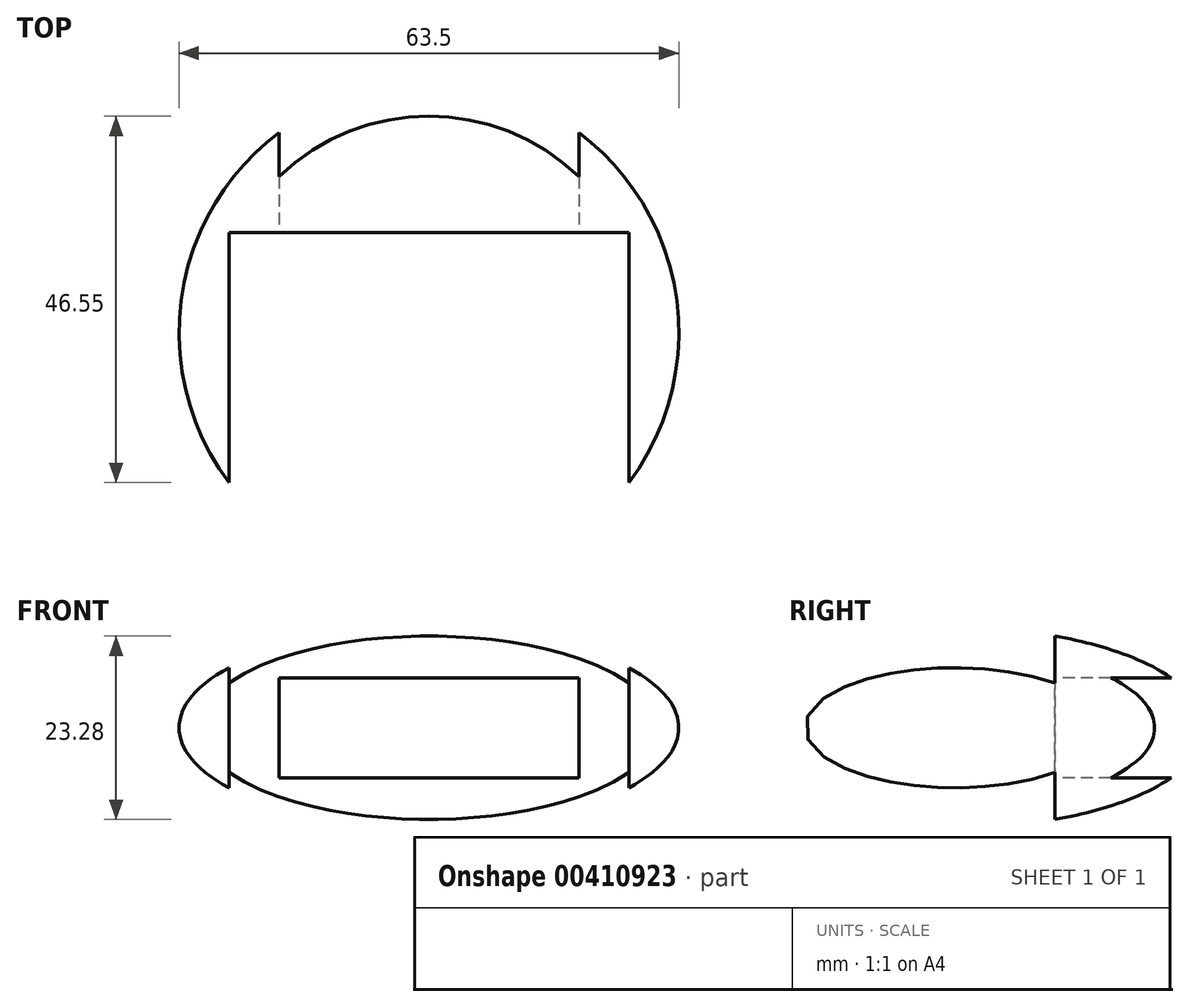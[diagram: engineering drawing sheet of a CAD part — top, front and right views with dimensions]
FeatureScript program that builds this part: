
annotation { "Feature Type Name" : "Feature", "Feature Type Description" : "" }
export const myFeature = defineFeature(function(context is Context, id is Id, definition is map)
    precondition{}
    {
        {
            var Q0;
            Q0=qCreatedBy(makeId("Front.planeOp"),FACE);
            var sketch = newSketch(context, id + "F0", { "sketchPlane" : qUnion([Q0])});
            skEllipticalArc(sketch, "E0", {});
            skLineSegment(sketch, "E1", {"start": v(0, 12.7) * mm, "end": v(0, -12.7) * mm, "construction": true});
            skLineSegment(sketch, "E2", {"start": v(0, 12.7) * mm, "end": v(0, -12.7) * mm});
            const initialGuessF0  = {"E0": [0, 0, -1, 0, 0.03175, 0.0127, 1.5707963267948966, 4.71238898038469]};
            skSetInitialGuess(sketch, initialGuessF0);
            skSolve(sketch);
        }
        {
            var Q0;
            Q0=makeQuery(id+"F0.imprint","IMPRINT",FACE,{"disambiguationData":[TD([[makeQuery(id+"F0.imprint","IMPRINT",EDGE,{"derivedFrom":sQuery(id+"F0.wireOp",EDGE,"E0")}),1.0]])]});
            var Q1;
            Q1=sQuery(id+"F0.wireOp",EDGE,"E2");
            revolve(context, id + "F1", {"entities" : qUnion([Q0]), "axis" : qUnion([Q1]), "revolveType" : RevolveType.FULL});
        }
        {
            var Q0;
            Q0=qCreatedBy(makeId("Top.planeOp"),FACE);
            var sketch = newSketch(context, id + "F2", { "sketchPlane" : qUnion([Q0])});
            skLineSegment(sketch, "E3.bottom", {"start": v(25.4, 12.7) * mm, "end": v(-25.4, 12.7) * mm});
            skLineSegment(sketch, "E3.top", {"start": v(25.4, -38.1) * mm, "end": v(-25.4, -38.1) * mm});
            skLineSegment(sketch, "E3.left", {"start": v(25.4, 12.7) * mm, "end": v(25.4, -38.1) * mm});
            skLineSegment(sketch, "E3.right", {"start": v(-25.4, 12.7) * mm, "end": v(-25.4, -38.1) * mm});
            skSolve(sketch);
        }
        {
            var Q0;
            Q0 = qSketchRegion(id + "F2", true);
            extrude(context, id + "F3", {"entities" : qUnion([Q0]), "operationType" : NewBodyOperationType.REMOVE, "endBound" : BoundingType.SYMMETRIC, "oppositeDirection" : true, "depth" : 25.4 * mm});
        }
        {
            var Q0;
            Q0=makeQuery(id+"F3.boolean.opBoolean","COPY",FACE,{"derivedFrom":makeQuery(id+"F3.opExtrude","SWEPT_FACE",FACE,{"disambiguationData":[OSD([sQuery(id+"F2.wireOp",EDGE,"E3.bottom")])]})});
            var sketch = newSketch(context, id + "F4", { "sketchPlane" : qUnion([Q0])});
            skLineSegment(sketch, "E4.bottom", {"start": v(-19.05, 6.35) * mm, "end": v(19.05, 6.35) * mm});
            skLineSegment(sketch, "E4.top", {"start": v(-19.05, -6.35) * mm, "end": v(19.05, -6.35) * mm});
            skLineSegment(sketch, "E4.left", {"start": v(-19.05, 6.35) * mm, "end": v(-19.05, -6.35) * mm});
            skLineSegment(sketch, "E4.right", {"start": v(19.05, 6.35) * mm, "end": v(19.05, -6.35) * mm});
            skSolve(sketch);
        }
        {
            var Q0;
            Q0 = qSketchRegion(id + "F4", true);
            extrude(context, id + "F5", {"entities" : qUnion([Q0]), "operationType" : NewBodyOperationType.REMOVE, "oppositeDirection" : true, "depth" : 25.4 * mm});
        }
    });
